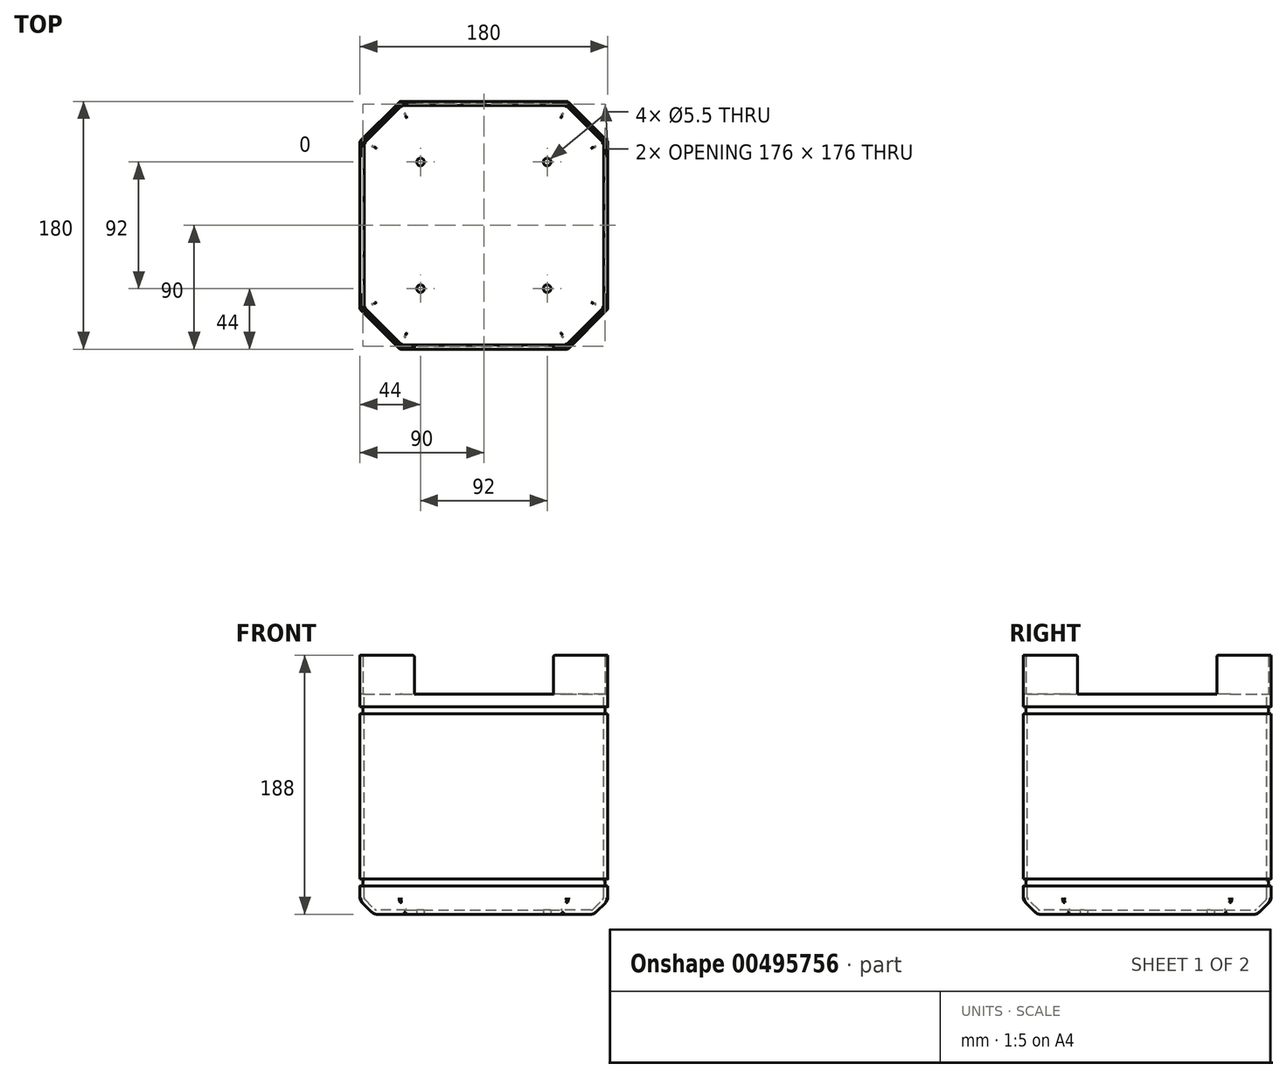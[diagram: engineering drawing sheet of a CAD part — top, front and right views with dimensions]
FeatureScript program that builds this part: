
annotation { "Feature Type Name" : "Feature", "Feature Type Description" : "" }
export const myFeature = defineFeature(function(context is Context, id is Id, definition is map)
    precondition{}
    {
        {
            var Q0;
            Q0=qCreatedBy(makeId("Top.planeOp"),FACE);
            var sketch = newSketch(context, id + "F0", { "sketchPlane" : qUnion([Q0])});
            skLineSegment(sketch, "E0.bottom", {"start": v(-61, 90) * mm, "end": v(61, 90) * mm});
            skLineSegment(sketch, "E0.top", {"start": v(-61, -90) * mm, "end": v(61, -90) * mm});
            skLineSegment(sketch, "E0.left", {"start": v(-90, 61) * mm, "end": v(-90, -61) * mm});
            skLineSegment(sketch, "E0.right", {"start": v(90, 61) * mm, "end": v(90, -61) * mm});
            skLineSegment(sketch, "E1", {"start": v(0, 156.9) * mm, "end": v(0, -146.72) * mm, "construction": true});
            skLineSegment(sketch, "E2", {"start": v(-149.43, 0) * mm, "end": v(169.81, 0) * mm, "construction": true});
            skLineSegment(sketch, "E3", {"start": v(-90, 61) * mm, "end": v(-61, 90) * mm});
            skLineSegment(sketch, "E4", {"start": v(-90, -61) * mm, "end": v(-61, -90) * mm});
            skLineSegment(sketch, "E5", {"start": v(61, -90) * mm, "end": v(90, -61) * mm});
            skLineSegment(sketch, "E6", {"start": v(61, 90) * mm, "end": v(90, 61) * mm});
            skPoint(sketch, "E7.orphan", {"position": v(-90, 90) * mm});
            skPoint(sketch, "E8.orphan", {"position": v(90, 90) * mm});
            skPoint(sketch, "E9.orphan", {"position": v(90, -90) * mm});
            skPoint(sketch, "E10.orphan", {"position": v(-90, -90) * mm});
            skSolve(sketch);
        }
        {
            var Q0;
            Q0=qSketchRegion(id+"F0",true);
            extrude(context, id + "F1", {"entities" : qUnion([Q0]), "depth" : 160 * mm, "offsetDistance" : 25 * mm});
        }
        {
            var Q0;
            Q0=makeQuery(id+"F1.opExtrude","CAP_EDGE",EDGE,{"disambiguationData":[OSD([sQuery(id+"F0.wireOp",EDGE,"E0.top")])],"isStart":true});
            var Q1;
            Q1=makeQuery(id+"F1.opExtrude","CAP_EDGE",EDGE,{"disambiguationData":[OSD([sQuery(id+"F0.wireOp",EDGE,"E4")])],"isStart":true});
            var Q2;
            Q2=makeQuery(id+"F1.opExtrude","CAP_EDGE",EDGE,{"disambiguationData":[OSD([sQuery(id+"F0.wireOp",EDGE,"E0.left")])],"isStart":true});
            var Q3;
            Q3=makeQuery(id+"F1.opExtrude","CAP_EDGE",EDGE,{"disambiguationData":[OSD([sQuery(id+"F0.wireOp",EDGE,"E3")])],"isStart":true});
            var Q4;
            Q4=makeQuery(id+"F1.opExtrude","CAP_EDGE",EDGE,{"disambiguationData":[OSD([sQuery(id+"F0.wireOp",EDGE,"E0.bottom")])],"isStart":true});
            var Q5;
            Q5=makeQuery(id+"F1.opExtrude","CAP_EDGE",EDGE,{"disambiguationData":[OSD([sQuery(id+"F0.wireOp",EDGE,"E6")])],"isStart":true});
            var Q6;
            Q6=makeQuery(id+"F1.opExtrude","CAP_EDGE",EDGE,{"disambiguationData":[OSD([sQuery(id+"F0.wireOp",EDGE,"E0.right")])],"isStart":true});
            var Q7;
            Q7=makeQuery(id+"F1.opExtrude","CAP_EDGE",EDGE,{"disambiguationData":[OSD([sQuery(id+"F0.wireOp",EDGE,"E5")])],"isStart":true});
            chamfer(context, id + "F2", {"entities" : qUnion([Q0, Q1, Q2, Q3, Q4, Q5, Q6, Q7]), "chamferType" : ChamferType.TWO_OFFSETS, "width1" : 10 * mm, "oppositeDirection" : true, "width2" : 10 * mm, "tangentPropagation" : true});
        }
        {
            var Q0;
            Q0=makeQuery(id+"F1.opExtrude","CAP_FACE",FACE,{"disambiguationData":[OSD([sQuery(id+"F0.wireOp",EDGE,"E0.bottom"),sQuery(id+"F0.wireOp",EDGE,"E0.top"),sQuery(id+"F0.wireOp",EDGE,"E0.left"),sQuery(id+"F0.wireOp",EDGE,"E0.right"),sQuery(id+"F0.wireOp",EDGE,"E3"),sQuery(id+"F0.wireOp",EDGE,"E4"),sQuery(id+"F0.wireOp",EDGE,"E5"),sQuery(id+"F0.wireOp",EDGE,"E6")])],"isStart":false});
            var sketch = newSketch(context, id + "F3", { "sketchPlane" : qUnion([Q0])});
            skLineSegment(sketch, "E11", {"start": v(90, -61) * mm, "end": v(61, -90) * mm});
            skLineSegment(sketch, "E12.0", {"start": v(88, -60.17) * mm, "end": v(60.17, -88) * mm});
            skLineSegment(sketch, "E13", {"start": v(90, -61) * mm, "end": v(90, -90) * mm, "construction": true});
            skLineSegment(sketch, "E14", {"start": v(90, -90) * mm, "end": v(61, -90) * mm, "construction": true});
            skLineSegment(sketch, "E15", {"start": v(90, -61) * mm, "end": v(90, -50.5) * mm});
            skLineSegment(sketch, "E16", {"start": v(61, -90) * mm, "end": v(50.5, -90) * mm});
            skLineSegment(sketch, "E17.0", {"start": v(60.17, -88) * mm, "end": v(50.5, -88) * mm});
            skLineSegment(sketch, "E18.0", {"start": v(88, -60.17) * mm, "end": v(88, -50.5) * mm});
            skLineSegment(sketch, "E19", {"start": v(88, -50.5) * mm, "end": v(90, -50.5) * mm});
            skLineSegment(sketch, "E20", {"start": v(50.5, -88) * mm, "end": v(50.5, -90) * mm});
            skLineSegment(sketch, "E21", {"start": v(104.54, 0) * mm, "end": v(-130.04, 0) * mm, "construction": true});
            skPoint(sketch, "E21.endSnap0", {"position": v(-90, 0) * mm});
            skLineSegment(sketch, "E22", {"start": v(0, 121.87) * mm, "end": v(0, -139.26) * mm, "construction": true});
            skLineSegment(sketch, "E23.MirrorCS", {"start": v(88, 50.5) * mm, "end": v(90, 50.5) * mm});
            skLineSegment(sketch, "E24.MirrorCS", {"start": v(50.5, 88) * mm, "end": v(50.5, 90) * mm});
            skLineSegment(sketch, "E25.MirrorCS", {"start": v(61, 90) * mm, "end": v(50.5, 90) * mm});
            skLineSegment(sketch, "E26.MirrorCS", {"start": v(60.17, 88) * mm, "end": v(50.5, 88) * mm});
            skLineSegment(sketch, "E27.MirrorCS", {"start": v(88, 60.17) * mm, "end": v(88, 50.5) * mm});
            skLineSegment(sketch, "E28.MirrorCS", {"start": v(90, 61) * mm, "end": v(90, 50.5) * mm});
            skLineSegment(sketch, "E29.MirrorCS", {"start": v(90, 61) * mm, "end": v(61, 90) * mm});
            skLineSegment(sketch, "E30.MirrorCS", {"start": v(88, 60.17) * mm, "end": v(60.17, 88) * mm});
            skLineSegment(sketch, "E31.MirrorCS", {"start": v(90, 90) * mm, "end": v(61, 90) * mm, "construction": true});
            skLineSegment(sketch, "E32.MirrorCS", {"start": v(90, 61) * mm, "end": v(90, 90) * mm, "construction": true});
            skLineSegment(sketch, "E33.MirrorCS", {"start": v(-88, 50.5) * mm, "end": v(-90, 50.5) * mm});
            skLineSegment(sketch, "E34.MirrorCS", {"start": v(-50.5, 88) * mm, "end": v(-50.5, 90) * mm});
            skLineSegment(sketch, "E35.MirrorCS", {"start": v(-88, -50.5) * mm, "end": v(-90, -50.5) * mm});
            skLineSegment(sketch, "E36.MirrorCS", {"start": v(-50.5, -88) * mm, "end": v(-50.5, -90) * mm});
            skLineSegment(sketch, "E37.MirrorCS", {"start": v(-61, -90) * mm, "end": v(-50.5, -90) * mm});
            skLineSegment(sketch, "E38.MirrorCS", {"start": v(-88, 60.17) * mm, "end": v(-88, 50.5) * mm});
            skLineSegment(sketch, "E39.MirrorCS", {"start": v(-61, 90) * mm, "end": v(-50.5, 90) * mm});
            skLineSegment(sketch, "E40.MirrorCS", {"start": v(-88, 60.17) * mm, "end": v(-60.17, 88) * mm});
            skLineSegment(sketch, "E41.MirrorCS", {"start": v(-88, -60.17) * mm, "end": v(-88, -50.5) * mm});
            skLineSegment(sketch, "E42.MirrorCS", {"start": v(-90, 61) * mm, "end": v(-61, 90) * mm});
            skLineSegment(sketch, "E43.MirrorCS", {"start": v(-60.17, 88) * mm, "end": v(-50.5, 88) * mm});
            skLineSegment(sketch, "E44.MirrorCS", {"start": v(-90, 61) * mm, "end": v(-90, 50.5) * mm});
            skLineSegment(sketch, "E45.MirrorCS", {"start": v(-90, -61) * mm, "end": v(-90, -50.5) * mm});
            skLineSegment(sketch, "E46.MirrorCS", {"start": v(-60.17, -88) * mm, "end": v(-50.5, -88) * mm});
            skLineSegment(sketch, "E47.MirrorCS", {"start": v(-90, 90) * mm, "end": v(-61, 90) * mm, "construction": true});
            skLineSegment(sketch, "E48.MirrorCS", {"start": v(-90, 61) * mm, "end": v(-90, 90) * mm, "construction": true});
            skLineSegment(sketch, "E49.MirrorCS", {"start": v(-90, -61) * mm, "end": v(-61, -90) * mm});
            skLineSegment(sketch, "E50.MirrorCS", {"start": v(-90, -61) * mm, "end": v(-90, -90) * mm, "construction": true});
            skLineSegment(sketch, "E51.MirrorCS", {"start": v(-90, -90) * mm, "end": v(-61, -90) * mm, "construction": true});
            skLineSegment(sketch, "E52.MirrorCS", {"start": v(-88, -60.17) * mm, "end": v(-60.17, -88) * mm});
            skSolve(sketch);
        }
        {
            var Q0;
            Q0=qSketchRegion(id+"F3",true);
            extrude(context, id + "F4", {"entities" : qUnion([Q0]), "operationType" : NewBodyOperationType.ADD, "depth" : 28 * mm});
        }
        {
            var Q0;
            {var subQ0=sQuery(id+"F0.wireOp",EDGE,"E6");Q0=makeQuery(id+"F2.opChamfer","BLEND_EDGE",EDGE,{"blendedFrom":[makeQuery(id+"F1.opExtrude","CAP_EDGE",EDGE,{"disambiguationData":[OSD([subQ0])],"isStart":true}),makeQuery(id+"F1.opExtrude","SWEPT_FACE",FACE,{"disambiguationData":[OSD([subQ0])]})],"blendedInto":[makeQuery(id+"F1.opExtrude","SWEPT_FACE",FACE,{"disambiguationData":[OSD([subQ0])]})]});}
            var Q1;
            {var subQ0=sQuery(id+"F0.wireOp",EDGE,"E0.right");Q1=makeQuery(id+"F2.opChamfer","BLEND_EDGE",EDGE,{"blendedFrom":[makeQuery(id+"F1.opExtrude","CAP_EDGE",EDGE,{"disambiguationData":[OSD([subQ0])],"isStart":true}),makeQuery(id+"F1.opExtrude","SWEPT_FACE",FACE,{"disambiguationData":[OSD([subQ0])]})],"blendedInto":[makeQuery(id+"F1.opExtrude","SWEPT_FACE",FACE,{"disambiguationData":[OSD([subQ0])]})]});}
            var Q2;
            {var subQ0=sQuery(id+"F0.wireOp",EDGE,"E5");Q2=makeQuery(id+"F2.opChamfer","BLEND_EDGE",EDGE,{"blendedFrom":[makeQuery(id+"F1.opExtrude","CAP_EDGE",EDGE,{"disambiguationData":[OSD([subQ0])],"isStart":true}),makeQuery(id+"F1.opExtrude","SWEPT_FACE",FACE,{"disambiguationData":[OSD([subQ0])]})],"blendedInto":[makeQuery(id+"F1.opExtrude","SWEPT_FACE",FACE,{"disambiguationData":[OSD([subQ0])]})]});}
            var Q3;
            {var subQ0=sQuery(id+"F0.wireOp",EDGE,"E0.top");Q3=makeQuery(id+"F2.opChamfer","BLEND_EDGE",EDGE,{"blendedFrom":[makeQuery(id+"F1.opExtrude","CAP_EDGE",EDGE,{"disambiguationData":[OSD([subQ0])],"isStart":true}),makeQuery(id+"F1.opExtrude","SWEPT_FACE",FACE,{"disambiguationData":[OSD([subQ0])]})],"blendedInto":[makeQuery(id+"F1.opExtrude","SWEPT_FACE",FACE,{"disambiguationData":[OSD([subQ0])]})]});}
            var Q4;
            {var subQ0=sQuery(id+"F0.wireOp",EDGE,"E4");Q4=makeQuery(id+"F2.opChamfer","BLEND_EDGE",EDGE,{"blendedFrom":[makeQuery(id+"F1.opExtrude","CAP_EDGE",EDGE,{"disambiguationData":[OSD([subQ0])],"isStart":true}),makeQuery(id+"F1.opExtrude","SWEPT_FACE",FACE,{"disambiguationData":[OSD([subQ0])]})],"blendedInto":[makeQuery(id+"F1.opExtrude","SWEPT_FACE",FACE,{"disambiguationData":[OSD([subQ0])]})]});}
            var Q5;
            {var subQ0=sQuery(id+"F0.wireOp",EDGE,"E0.left");Q5=makeQuery(id+"F2.opChamfer","BLEND_EDGE",EDGE,{"blendedFrom":[makeQuery(id+"F1.opExtrude","CAP_EDGE",EDGE,{"disambiguationData":[OSD([subQ0])],"isStart":true}),makeQuery(id+"F1.opExtrude","SWEPT_FACE",FACE,{"disambiguationData":[OSD([subQ0])]})],"blendedInto":[makeQuery(id+"F1.opExtrude","SWEPT_FACE",FACE,{"disambiguationData":[OSD([subQ0])]})]});}
            var Q6;
            {var subQ0=sQuery(id+"F0.wireOp",EDGE,"E3");Q6=makeQuery(id+"F2.opChamfer","BLEND_EDGE",EDGE,{"blendedFrom":[makeQuery(id+"F1.opExtrude","CAP_EDGE",EDGE,{"disambiguationData":[OSD([subQ0])],"isStart":true}),makeQuery(id+"F1.opExtrude","SWEPT_FACE",FACE,{"disambiguationData":[OSD([subQ0])]})],"blendedInto":[makeQuery(id+"F1.opExtrude","SWEPT_FACE",FACE,{"disambiguationData":[OSD([subQ0])]})]});}
            var Q7;
            {var subQ0=sQuery(id+"F0.wireOp",EDGE,"E0.bottom");Q7=makeQuery(id+"F2.opChamfer","BLEND_EDGE",EDGE,{"blendedFrom":[makeQuery(id+"F1.opExtrude","CAP_EDGE",EDGE,{"disambiguationData":[OSD([subQ0])],"isStart":true}),makeQuery(id+"F1.opExtrude","SWEPT_FACE",FACE,{"disambiguationData":[OSD([subQ0])]})],"blendedInto":[makeQuery(id+"F1.opExtrude","SWEPT_FACE",FACE,{"disambiguationData":[OSD([subQ0])]})]});}
            fillet(context, id + "F5", {"entities" : qUnion([Q0, Q1, Q2, Q3, Q4, Q5, Q6, Q7]), "radius" : 5 * mm, "tangentPropagation" : true, "allowEdgeOverflow" : false});
        }
        {
            var Q0;
            Q0=makeQuery(id+"F4.boolean.opBoolean","MERGE",EDGE,{"derivedFrom":[makeQuery(id+"F1.opExtrude","SWEPT_EDGE",EDGE,{"disambiguationData":[OSD([sQuery(id+"F0.wireOp",EDGE,"E0.bottom"),sQuery(id+"F0.wireOp",EDGE,"E6")])]}),makeQuery(id+"F4.opExtrude","SWEPT_EDGE",EDGE,{"disambiguationData":[OSD([sQuery(id+"F3.wireOp",EDGE,"E25.MirrorCS"),sQuery(id+"F3.wireOp",EDGE,"E29.MirrorCS")])]})]});
            var Q1;
            Q1=makeQuery(id+"F4.boolean.opBoolean","MERGE",EDGE,{"derivedFrom":[makeQuery(id+"F1.opExtrude","SWEPT_EDGE",EDGE,{"disambiguationData":[OSD([sQuery(id+"F0.wireOp",EDGE,"E0.right"),sQuery(id+"F0.wireOp",EDGE,"E6")])]}),makeQuery(id+"F4.opExtrude","SWEPT_EDGE",EDGE,{"disambiguationData":[OSD([sQuery(id+"F3.wireOp",EDGE,"E28.MirrorCS"),sQuery(id+"F3.wireOp",EDGE,"E29.MirrorCS")])]})]});
            var Q2;
            Q2=makeQuery(id+"F4.boolean.opBoolean","MERGE",EDGE,{"derivedFrom":[makeQuery(id+"F1.opExtrude","SWEPT_EDGE",EDGE,{"disambiguationData":[OSD([sQuery(id+"F0.wireOp",EDGE,"E0.bottom"),sQuery(id+"F0.wireOp",EDGE,"E3")])]}),makeQuery(id+"F4.opExtrude","SWEPT_EDGE",EDGE,{"disambiguationData":[OSD([sQuery(id+"F3.wireOp",EDGE,"E39.MirrorCS"),sQuery(id+"F3.wireOp",EDGE,"E42.MirrorCS")])]})]});
            var Q3;
            Q3=makeQuery(id+"F4.boolean.opBoolean","MERGE",EDGE,{"derivedFrom":[makeQuery(id+"F1.opExtrude","SWEPT_EDGE",EDGE,{"disambiguationData":[OSD([sQuery(id+"F0.wireOp",EDGE,"E0.right"),sQuery(id+"F0.wireOp",EDGE,"E5")])]}),makeQuery(id+"F4.opExtrude","SWEPT_EDGE",EDGE,{"disambiguationData":[OSD([sQuery(id+"F3.wireOp",EDGE,"E11"),sQuery(id+"F3.wireOp",EDGE,"E15")])]})]});
            var Q4;
            Q4=makeQuery(id+"F2.opChamfer","BLEND_EDGE",EDGE,{"blendedFrom":[makeQuery(id+"F1.opExtrude","CAP_EDGE",EDGE,{"disambiguationData":[OSD([sQuery(id+"F0.wireOp",EDGE,"E0.top")])],"isStart":true}),makeQuery(id+"F1.opExtrude","CAP_EDGE",EDGE,{"disambiguationData":[OSD([sQuery(id+"F0.wireOp",EDGE,"E5")])],"isStart":true})],"blendedInto":[]});
            var Q5;
            Q5=makeQuery(id+"F2.opChamfer","BLEND_EDGE",EDGE,{"blendedFrom":[makeQuery(id+"F1.opExtrude","CAP_EDGE",EDGE,{"disambiguationData":[OSD([sQuery(id+"F0.wireOp",EDGE,"E0.top")])],"isStart":true}),makeQuery(id+"F1.opExtrude","CAP_EDGE",EDGE,{"disambiguationData":[OSD([sQuery(id+"F0.wireOp",EDGE,"E4")])],"isStart":true})],"blendedInto":[]});
            var Q6;
            Q6=makeQuery(id+"F2.opChamfer","BLEND_EDGE",EDGE,{"blendedFrom":[makeQuery(id+"F1.opExtrude","CAP_EDGE",EDGE,{"disambiguationData":[OSD([sQuery(id+"F0.wireOp",EDGE,"E0.left")])],"isStart":true}),makeQuery(id+"F1.opExtrude","CAP_EDGE",EDGE,{"disambiguationData":[OSD([sQuery(id+"F0.wireOp",EDGE,"E4")])],"isStart":true})],"blendedInto":[]});
            var Q7;
            Q7=makeQuery(id+"F2.opChamfer","BLEND_EDGE",EDGE,{"blendedFrom":[makeQuery(id+"F1.opExtrude","CAP_EDGE",EDGE,{"disambiguationData":[OSD([sQuery(id+"F0.wireOp",EDGE,"E0.left")])],"isStart":true}),makeQuery(id+"F1.opExtrude","CAP_EDGE",EDGE,{"disambiguationData":[OSD([sQuery(id+"F0.wireOp",EDGE,"E3")])],"isStart":true})],"blendedInto":[]});
            fillet(context, id + "F6", {"entities" : qUnion([Q0, Q1, Q2, Q3, Q4, Q5, Q6, Q7]), "radius" : 2 * mm, "tangentPropagation" : true, "allowEdgeOverflow" : false});
        }
        {
            var Q0;
            {var subQ0=sQuery(id+"F0.wireOp",EDGE,"E0.left");Q0=makeQuery(id+"F2.opChamfer","BLEND_EDGE",EDGE,{"blendedFrom":[makeQuery(id+"F1.opExtrude","CAP_EDGE",EDGE,{"disambiguationData":[OSD([subQ0])],"isStart":true}),makeQuery(id+"F1.opExtrude","CAP_FACE",FACE,{"disambiguationData":[OSD([sQuery(id+"F0.wireOp",EDGE,"E0.bottom"),sQuery(id+"F0.wireOp",EDGE,"E0.top"),subQ0,sQuery(id+"F0.wireOp",EDGE,"E0.right"),sQuery(id+"F0.wireOp",EDGE,"E3"),sQuery(id+"F0.wireOp",EDGE,"E4"),sQuery(id+"F0.wireOp",EDGE,"E5"),sQuery(id+"F0.wireOp",EDGE,"E6")])],"isStart":true})],"blendedInto":[makeQuery(id+"F1.opExtrude","CAP_FACE",FACE,{"disambiguationData":[OSD([sQuery(id+"F0.wireOp",EDGE,"E0.bottom"),sQuery(id+"F0.wireOp",EDGE,"E0.top"),subQ0,sQuery(id+"F0.wireOp",EDGE,"E0.right"),sQuery(id+"F0.wireOp",EDGE,"E3"),sQuery(id+"F0.wireOp",EDGE,"E4"),sQuery(id+"F0.wireOp",EDGE,"E5"),sQuery(id+"F0.wireOp",EDGE,"E6")])],"isStart":true})]});}
            fillet(context, id + "F7", {"entities" : qUnion([Q0]), "radius" : 5 * mm, "tangentPropagation" : true, "allowEdgeOverflow" : false});
        }
        {
            var Q0;
            Q0=makeQuery(id+"F1.opExtrude","CAP_FACE",FACE,{"disambiguationData":[OSD([sQuery(id+"F0.wireOp",EDGE,"E0.bottom"),sQuery(id+"F0.wireOp",EDGE,"E0.top"),sQuery(id+"F0.wireOp",EDGE,"E0.left"),sQuery(id+"F0.wireOp",EDGE,"E0.right"),sQuery(id+"F0.wireOp",EDGE,"E3"),sQuery(id+"F0.wireOp",EDGE,"E4"),sQuery(id+"F0.wireOp",EDGE,"E5"),sQuery(id+"F0.wireOp",EDGE,"E6")])],"isStart":false});
            shell(context, id + "F8", {"entities" : qUnion([Q0]), "thickness" : 3 * mm});
        }
        {
            var Q0;
            Q0=qCreatedBy(makeId("Front.planeOp"),FACE);
            var sketch = newSketch(context, id + "F9", { "sketchPlane" : qUnion([Q0])});
            skLineSegment(sketch, "E53.bottom", {"start": v(109.07, 145.57) * mm, "end": v(-112.92, 145.57) * mm});
            skLineSegment(sketch, "E53.top", {"start": v(109.07, 150.57) * mm, "end": v(-112.92, 150.57) * mm});
            skLineSegment(sketch, "E53.left", {"start": v(109.07, 145.57) * mm, "end": v(109.07, 150.57) * mm});
            skLineSegment(sketch, "E53.right", {"start": v(-112.92, 145.57) * mm, "end": v(-112.92, 150.57) * mm});
            skLineSegment(sketch, "E54.bottom", {"start": v(124, 20.57) * mm, "end": v(-129.94, 20.57) * mm});
            skLineSegment(sketch, "E54.top", {"start": v(124, 25.57) * mm, "end": v(-129.94, 25.57) * mm});
            skLineSegment(sketch, "E54.left", {"start": v(124, 20.57) * mm, "end": v(124, 25.57) * mm});
            skLineSegment(sketch, "E54.right", {"start": v(-129.94, 20.57) * mm, "end": v(-129.94, 25.57) * mm});
            skSolve(sketch);
        }
        {
            var Q0;
            Q0 = qSketchRegion(id + "F9", true);
            extrude(context, id + "F10", {"entities" : qUnion([Q0]), "operationType" : NewBodyOperationType.REMOVE, "oppositeDirection" : true, "depth" : 180 * mm, "symmetric" : true});
        }
        {
            var Q0;
            Q0=makeQuery(id+"F10.boolean.opBoolean","COPY",FACE,{"derivedFrom":makeQuery(id+"F10.opExtrude","SWEPT_FACE",FACE,{"disambiguationData":[OSD([sQuery(id+"F9.wireOp",EDGE,"E54.bottom")])]})});
            var sketch = newSketch(context, id + "F11", { "sketchPlane" : qUnion([Q0])});
            skLineSegment(sketch, "E55.0", {"start": v(-60.17, -88) * mm, "end": v(60.17, -88) * mm});
            skLineSegment(sketch, "E55.1", {"start": v(-88, -60.17) * mm, "end": v(-60.17, -88) * mm});
            skLineSegment(sketch, "E55.2", {"start": v(60.17, -88) * mm, "end": v(88, -60.17) * mm});
            skLineSegment(sketch, "E55.3", {"start": v(-88, 60.17) * mm, "end": v(-88, -60.17) * mm});
            skLineSegment(sketch, "E55.4", {"start": v(88, -60.17) * mm, "end": v(88, 60.17) * mm});
            skLineSegment(sketch, "E55.5", {"start": v(88, 60.17) * mm, "end": v(60.17, 88) * mm});
            skLineSegment(sketch, "E55.6", {"start": v(60.17, 88) * mm, "end": v(-60.17, 88) * mm});
            skLineSegment(sketch, "E55.7", {"start": v(-60.17, 88) * mm, "end": v(-88, 60.17) * mm});
            skLineSegment(sketch, "E56.0", {"start": v(-59.76, 87) * mm, "end": v(-59.76, 87) * mm});
            skLineSegment(sketch, "E56.2", {"start": v(-87, 59.76) * mm, "end": v(-87, -59.76) * mm});
            skLineSegment(sketch, "E56.4", {"start": v(-59.76, 87) * mm, "end": v(59.76, 87) * mm});
            skLineSegment(sketch, "E56.6", {"start": v(59.76, 87) * mm, "end": v(59.76, 87) * mm});
            skLineSegment(sketch, "E56.8", {"start": v(87, 59.76) * mm, "end": v(87, -59.76) * mm});
            skLineSegment(sketch, "E56.10", {"start": v(59.76, -87) * mm, "end": v(59.76, -87) * mm});
            skLineSegment(sketch, "E56.12", {"start": v(-59.76, -87) * mm, "end": v(59.76, -87) * mm});
            skLineSegment(sketch, "E56.14", {"start": v(-59.76, -87) * mm, "end": v(-59.76, -87) * mm});
            skLineSegment(sketch, "E57", {"start": v(87, 59.76) * mm, "end": v(59.76, 87) * mm});
            skLineSegment(sketch, "E58", {"start": v(-59.76, 87) * mm, "end": v(-87, 59.76) * mm});
            skLineSegment(sketch, "E59", {"start": v(-59.76, -87) * mm, "end": v(-87, -59.76) * mm});
            skLineSegment(sketch, "E60", {"start": v(87, -59.76) * mm, "end": v(59.76, -87) * mm});
            skSolve(sketch);
        }
        {
            var Q0;
            Q0 = qSketchRegion(id + "F11", true);
            extrude(context, id + "F12", {"entities" : qUnion([Q0]), "operationType" : NewBodyOperationType.ADD, "depth" : 130 * mm});
        }
        {
            var Q0;
            {var subQ0=sQuery(id+"F11.wireOp",EDGE,"E55.7");var subQ1=sQuery(id+"F11.wireOp",EDGE,"E55.3");Q0=makeQuery(id+"F12.boolean.opBoolean","SPLIT",EDGE,{"disambiguationData":[TD([makeQuery(id+"F10.boolean.opBoolean","COPY",FACE,{"derivedFrom":makeQuery(id+"F10.opExtrude","SWEPT_FACE",FACE,{"disambiguationData":[OSD([sQuery(id+"F9.wireOp",EDGE,"E54.bottom")])]})})])],"derivedFrom":makeQuery(id+"F12.opExtrude","SWEPT_EDGE",EDGE,{"disambiguationData":[OSD([subQ1,subQ0])]})});}
            var Q1;
            {var subQ0=sQuery(id+"F11.wireOp",EDGE,"E55.7");var subQ1=sQuery(id+"F11.wireOp",EDGE,"E55.6");Q1=makeQuery(id+"F12.boolean.opBoolean","SPLIT",EDGE,{"disambiguationData":[TD([makeQuery(id+"F10.boolean.opBoolean","COPY",FACE,{"derivedFrom":makeQuery(id+"F10.opExtrude","SWEPT_FACE",FACE,{"disambiguationData":[OSD([sQuery(id+"F9.wireOp",EDGE,"E54.bottom")])]})})])],"derivedFrom":makeQuery(id+"F12.opExtrude","SWEPT_EDGE",EDGE,{"disambiguationData":[OSD([subQ1,subQ0])]})});}
            var Q2;
            {var subQ0=sQuery(id+"F11.wireOp",EDGE,"E55.5");var subQ1=sQuery(id+"F11.wireOp",EDGE,"E55.6");Q2=makeQuery(id+"F12.boolean.opBoolean","SPLIT",EDGE,{"disambiguationData":[TD([makeQuery(id+"F10.boolean.opBoolean","COPY",FACE,{"derivedFrom":makeQuery(id+"F10.opExtrude","SWEPT_FACE",FACE,{"disambiguationData":[OSD([sQuery(id+"F9.wireOp",EDGE,"E54.bottom")])]})})])],"derivedFrom":makeQuery(id+"F12.opExtrude","SWEPT_EDGE",EDGE,{"disambiguationData":[OSD([subQ0,subQ1])]})});}
            var Q3;
            {var subQ0=sQuery(id+"F11.wireOp",EDGE,"E55.5");var subQ1=sQuery(id+"F11.wireOp",EDGE,"E55.6");Q3=makeQuery(id+"F12.boolean.opBoolean","SPLIT",EDGE,{"disambiguationData":[TD([makeQuery(id+"F10.boolean.opBoolean","COPY",FACE,{"derivedFrom":makeQuery(id+"F10.opExtrude","SWEPT_FACE",FACE,{"disambiguationData":[OSD([sQuery(id+"F9.wireOp",EDGE,"E53.bottom")])]})})])],"derivedFrom":makeQuery(id+"F12.opExtrude","SWEPT_EDGE",EDGE,{"disambiguationData":[OSD([subQ0,subQ1])]})});}
            var Q4;
            {var subQ0=sQuery(id+"F11.wireOp",EDGE,"E55.6");var subQ1=sQuery(id+"F11.wireOp",EDGE,"E55.7");Q4=makeQuery(id+"F12.boolean.opBoolean","SPLIT",EDGE,{"disambiguationData":[TD([makeQuery(id+"F10.boolean.opBoolean","COPY",FACE,{"derivedFrom":makeQuery(id+"F10.opExtrude","SWEPT_FACE",FACE,{"disambiguationData":[OSD([sQuery(id+"F9.wireOp",EDGE,"E53.bottom")])]})})])],"derivedFrom":makeQuery(id+"F12.opExtrude","SWEPT_EDGE",EDGE,{"disambiguationData":[OSD([subQ0,subQ1])]})});}
            var Q5;
            {var subQ0=sQuery(id+"F11.wireOp",EDGE,"E55.3");var subQ1=sQuery(id+"F11.wireOp",EDGE,"E55.7");Q5=makeQuery(id+"F12.boolean.opBoolean","SPLIT",EDGE,{"disambiguationData":[TD([makeQuery(id+"F10.boolean.opBoolean","COPY",FACE,{"derivedFrom":makeQuery(id+"F10.opExtrude","SWEPT_FACE",FACE,{"disambiguationData":[OSD([sQuery(id+"F9.wireOp",EDGE,"E53.bottom")])]})})])],"derivedFrom":makeQuery(id+"F12.opExtrude","SWEPT_EDGE",EDGE,{"disambiguationData":[OSD([subQ0,subQ1])]})});}
            var Q6;
            {var subQ0=sQuery(id+"F11.wireOp",EDGE,"E55.5");var subQ1=sQuery(id+"F11.wireOp",EDGE,"E55.4");Q6=makeQuery(id+"F12.boolean.opBoolean","SPLIT",EDGE,{"disambiguationData":[TD([makeQuery(id+"F10.boolean.opBoolean","COPY",FACE,{"derivedFrom":makeQuery(id+"F10.opExtrude","SWEPT_FACE",FACE,{"disambiguationData":[OSD([sQuery(id+"F9.wireOp",EDGE,"E53.bottom")])]})})])],"derivedFrom":makeQuery(id+"F12.opExtrude","SWEPT_EDGE",EDGE,{"disambiguationData":[OSD([subQ1,subQ0])]})});}
            var Q7;
            {var subQ0=sQuery(id+"F11.wireOp",EDGE,"E55.4");var subQ1=sQuery(id+"F11.wireOp",EDGE,"E55.5");Q7=makeQuery(id+"F12.boolean.opBoolean","SPLIT",EDGE,{"disambiguationData":[TD([makeQuery(id+"F10.boolean.opBoolean","COPY",FACE,{"derivedFrom":makeQuery(id+"F10.opExtrude","SWEPT_FACE",FACE,{"disambiguationData":[OSD([sQuery(id+"F9.wireOp",EDGE,"E54.bottom")])]})})])],"derivedFrom":makeQuery(id+"F12.opExtrude","SWEPT_EDGE",EDGE,{"disambiguationData":[OSD([subQ0,subQ1])]})});}
            var Q8;
            {var subQ0=sQuery(id+"F11.wireOp",EDGE,"E55.2");var subQ1=sQuery(id+"F11.wireOp",EDGE,"E55.4");Q8=makeQuery(id+"F12.boolean.opBoolean","SPLIT",EDGE,{"disambiguationData":[TD([makeQuery(id+"F10.boolean.opBoolean","COPY",FACE,{"derivedFrom":makeQuery(id+"F10.opExtrude","SWEPT_FACE",FACE,{"disambiguationData":[OSD([sQuery(id+"F9.wireOp",EDGE,"E54.bottom")])]})})])],"derivedFrom":makeQuery(id+"F12.opExtrude","SWEPT_EDGE",EDGE,{"disambiguationData":[OSD([subQ0,subQ1])]})});}
            var Q9;
            {var subQ0=sQuery(id+"F11.wireOp",EDGE,"E55.2");var subQ1=sQuery(id+"F11.wireOp",EDGE,"E55.0");Q9=makeQuery(id+"F12.boolean.opBoolean","SPLIT",EDGE,{"disambiguationData":[TD([makeQuery(id+"F10.boolean.opBoolean","COPY",FACE,{"derivedFrom":makeQuery(id+"F10.opExtrude","SWEPT_FACE",FACE,{"disambiguationData":[OSD([sQuery(id+"F9.wireOp",EDGE,"E54.bottom")])]})})])],"derivedFrom":makeQuery(id+"F12.opExtrude","SWEPT_EDGE",EDGE,{"disambiguationData":[OSD([subQ1,subQ0])]})});}
            var Q10;
            {var subQ0=sQuery(id+"F11.wireOp",EDGE,"E55.2");var subQ1=sQuery(id+"F11.wireOp",EDGE,"E55.4");Q10=makeQuery(id+"F12.boolean.opBoolean","SPLIT",EDGE,{"disambiguationData":[TD([makeQuery(id+"F10.boolean.opBoolean","COPY",FACE,{"derivedFrom":makeQuery(id+"F10.opExtrude","SWEPT_FACE",FACE,{"disambiguationData":[OSD([sQuery(id+"F9.wireOp",EDGE,"E53.bottom")])]})})])],"derivedFrom":makeQuery(id+"F12.opExtrude","SWEPT_EDGE",EDGE,{"disambiguationData":[OSD([subQ0,subQ1])]})});}
            var Q11;
            {var subQ0=sQuery(id+"F11.wireOp",EDGE,"E55.0");var subQ1=sQuery(id+"F11.wireOp",EDGE,"E55.2");Q11=makeQuery(id+"F12.boolean.opBoolean","SPLIT",EDGE,{"disambiguationData":[TD([makeQuery(id+"F10.boolean.opBoolean","COPY",FACE,{"derivedFrom":makeQuery(id+"F10.opExtrude","SWEPT_FACE",FACE,{"disambiguationData":[OSD([sQuery(id+"F9.wireOp",EDGE,"E53.bottom")])]})})])],"derivedFrom":makeQuery(id+"F12.opExtrude","SWEPT_EDGE",EDGE,{"disambiguationData":[OSD([subQ0,subQ1])]})});}
            var Q12;
            {var subQ0=sQuery(id+"F11.wireOp",EDGE,"E55.0");var subQ1=sQuery(id+"F11.wireOp",EDGE,"E55.1");Q12=makeQuery(id+"F12.boolean.opBoolean","SPLIT",EDGE,{"disambiguationData":[TD([makeQuery(id+"F10.boolean.opBoolean","COPY",FACE,{"derivedFrom":makeQuery(id+"F10.opExtrude","SWEPT_FACE",FACE,{"disambiguationData":[OSD([sQuery(id+"F9.wireOp",EDGE,"E54.bottom")])]})})])],"derivedFrom":makeQuery(id+"F12.opExtrude","SWEPT_EDGE",EDGE,{"disambiguationData":[OSD([subQ0,subQ1])]})});}
            var Q13;
            {var subQ0=sQuery(id+"F11.wireOp",EDGE,"E55.3");var subQ1=sQuery(id+"F11.wireOp",EDGE,"E55.1");Q13=makeQuery(id+"F12.boolean.opBoolean","SPLIT",EDGE,{"disambiguationData":[TD([makeQuery(id+"F10.boolean.opBoolean","COPY",FACE,{"derivedFrom":makeQuery(id+"F10.opExtrude","SWEPT_FACE",FACE,{"disambiguationData":[OSD([sQuery(id+"F9.wireOp",EDGE,"E54.bottom")])]})})])],"derivedFrom":makeQuery(id+"F12.opExtrude","SWEPT_EDGE",EDGE,{"disambiguationData":[OSD([subQ1,subQ0])]})});}
            var Q14;
            {var subQ0=sQuery(id+"F11.wireOp",EDGE,"E55.1");var subQ1=sQuery(id+"F11.wireOp",EDGE,"E55.0");Q14=makeQuery(id+"F12.boolean.opBoolean","SPLIT",EDGE,{"disambiguationData":[TD([makeQuery(id+"F10.boolean.opBoolean","COPY",FACE,{"derivedFrom":makeQuery(id+"F10.opExtrude","SWEPT_FACE",FACE,{"disambiguationData":[OSD([sQuery(id+"F9.wireOp",EDGE,"E53.bottom")])]})})])],"derivedFrom":makeQuery(id+"F12.opExtrude","SWEPT_EDGE",EDGE,{"disambiguationData":[OSD([subQ1,subQ0])]})});}
            var Q15;
            {var subQ0=sQuery(id+"F11.wireOp",EDGE,"E55.1");var subQ1=sQuery(id+"F11.wireOp",EDGE,"E55.3");Q15=makeQuery(id+"F12.boolean.opBoolean","SPLIT",EDGE,{"disambiguationData":[TD([makeQuery(id+"F10.boolean.opBoolean","COPY",FACE,{"derivedFrom":makeQuery(id+"F10.opExtrude","SWEPT_FACE",FACE,{"disambiguationData":[OSD([sQuery(id+"F9.wireOp",EDGE,"E53.bottom")])]})})])],"derivedFrom":makeQuery(id+"F12.opExtrude","SWEPT_EDGE",EDGE,{"disambiguationData":[OSD([subQ0,subQ1])]})});}
            fillet(context, id + "F13", {"entities" : qUnion([Q0, Q1, Q2, Q3, Q4, Q5, Q6, Q7, Q8, Q9, Q10, Q11, Q12, Q13, Q14, Q15]), "radius" : 2 * mm, "tangentPropagation" : true, "allowEdgeOverflow" : false});
        }
        {
            var Q0;
            Q0=makeQuery(id+"F1.opExtrude","CAP_FACE",FACE,{"disambiguationData":[OSD([sQuery(id+"F0.wireOp",EDGE,"E0.bottom"),sQuery(id+"F0.wireOp",EDGE,"E0.top"),sQuery(id+"F0.wireOp",EDGE,"E0.left"),sQuery(id+"F0.wireOp",EDGE,"E0.right"),sQuery(id+"F0.wireOp",EDGE,"E3"),sQuery(id+"F0.wireOp",EDGE,"E4"),sQuery(id+"F0.wireOp",EDGE,"E5"),sQuery(id+"F0.wireOp",EDGE,"E6")])],"isStart":true});
            var sketch = newSketch(context, id + "F14", { "sketchPlane" : qUnion([Q0])});
            skLineSegment(sketch, "E61", {"start": v(0, 77.93) * mm, "end": v(0, -77.93) * mm, "construction": true});
            skLineSegment(sketch, "E62", {"start": v(-77.93, 0) * mm, "end": v(77.93, 0) * mm, "construction": true});
            skLineSegment(sketch, "E63", {"start": v(-66.96, -66.96) * mm, "end": v(66.96, 66.96) * mm, "construction": true});
            skLineSegment(sketch, "E64", {"start": v(-66.96, 66.96) * mm, "end": v(66.96, -66.96) * mm, "construction": true});
            skCircle(sketch, "E65", {"center": v(-46, -46) * mm, "radius": 2.75 * mm});
            skCircle(sketch, "E66", {"center": v(-46, 46) * mm, "radius": 2.75 * mm});
            skCircle(sketch, "E67", {"center": v(46, 46) * mm, "radius": 2.75 * mm});
            skCircle(sketch, "E68", {"center": v(46, -46) * mm, "radius": 2.75 * mm});
            skSolve(sketch);
        }
        {
            var Q0;
            Q0 = qSketchRegion(id + "F14", true);
            extrude(context, id + "F15", {"entities" : qUnion([Q0]), "operationType" : NewBodyOperationType.REMOVE, "oppositeDirection" : true, "depth" : 25 * mm});
        }
        {
            var Q0;
            Q0=makeQuery(id+"F4.opExtrude","SWEPT_EDGE",EDGE,{"disambiguationData":[OSD([sQuery(id+"F3.wireOp",EDGE,"E41.MirrorCS"),sQuery(id+"F3.wireOp",EDGE,"E52.MirrorCS")])]});
            var Q1;
            Q1=makeQuery(id+"F4.opExtrude","SWEPT_EDGE",EDGE,{"disambiguationData":[OSD([sQuery(id+"F3.wireOp",EDGE,"E46.MirrorCS"),sQuery(id+"F3.wireOp",EDGE,"E52.MirrorCS")])]});
            var Q2;
            Q2=makeQuery(id+"F4.opExtrude","SWEPT_EDGE",EDGE,{"disambiguationData":[OSD([sQuery(id+"F3.wireOp",EDGE,"E12.0"),sQuery(id+"F3.wireOp",EDGE,"E18.0")])]});
            var Q3;
            Q3=makeQuery(id+"F4.opExtrude","SWEPT_EDGE",EDGE,{"disambiguationData":[OSD([sQuery(id+"F3.wireOp",EDGE,"E12.0"),sQuery(id+"F3.wireOp",EDGE,"E17.0")])]});
            var Q4;
            Q4=makeQuery(id+"F4.opExtrude","SWEPT_EDGE",EDGE,{"disambiguationData":[OSD([sQuery(id+"F3.wireOp",EDGE,"E27.MirrorCS"),sQuery(id+"F3.wireOp",EDGE,"E30.MirrorCS")])]});
            var Q5;
            Q5=makeQuery(id+"F4.opExtrude","SWEPT_EDGE",EDGE,{"disambiguationData":[OSD([sQuery(id+"F3.wireOp",EDGE,"E26.MirrorCS"),sQuery(id+"F3.wireOp",EDGE,"E30.MirrorCS")])]});
            var Q6;
            Q6=makeQuery(id+"F4.opExtrude","SWEPT_EDGE",EDGE,{"disambiguationData":[OSD([sQuery(id+"F3.wireOp",EDGE,"E43.MirrorCS"),sQuery(id+"F3.wireOp",EDGE,"E40.MirrorCS")])]});
            var Q7;
            Q7=makeQuery(id+"F4.opExtrude","SWEPT_EDGE",EDGE,{"disambiguationData":[OSD([sQuery(id+"F3.wireOp",EDGE,"E38.MirrorCS"),sQuery(id+"F3.wireOp",EDGE,"E40.MirrorCS")])]});
            fillet(context, id + "F16", {"entities" : qUnion([Q0, Q1, Q2, Q3, Q4, Q5, Q6, Q7]), "radius" : 2 * mm, "tangentPropagation" : true, "allowEdgeOverflow" : false});
        }
        {
            var Q0;
            Q0=makeQuery(id+"F4.opExtrude","CAP_EDGE",EDGE,{"disambiguationData":[OSD([sQuery(id+"F3.wireOp",EDGE,"E35.MirrorCS")])],"isStart":false});
            var Q1;
            Q1=makeQuery(id+"F4.opExtrude","CAP_EDGE",EDGE,{"disambiguationData":[OSD([sQuery(id+"F3.wireOp",EDGE,"E36.MirrorCS")])],"isStart":false});
            var Q2;
            Q2=makeQuery(id+"F4.opExtrude","CAP_EDGE",EDGE,{"disambiguationData":[OSD([sQuery(id+"F3.wireOp",EDGE,"E20")])],"isStart":false});
            var Q3;
            Q3=makeQuery(id+"F4.opExtrude","CAP_EDGE",EDGE,{"disambiguationData":[OSD([sQuery(id+"F3.wireOp",EDGE,"E19")])],"isStart":false});
            var Q4;
            Q4=makeQuery(id+"F4.opExtrude","CAP_EDGE",EDGE,{"disambiguationData":[OSD([sQuery(id+"F3.wireOp",EDGE,"E23.MirrorCS")])],"isStart":false});
            var Q5;
            Q5=makeQuery(id+"F4.opExtrude","CAP_EDGE",EDGE,{"disambiguationData":[OSD([sQuery(id+"F3.wireOp",EDGE,"E24.MirrorCS")])],"isStart":false});
            var Q6;
            Q6=makeQuery(id+"F4.opExtrude","CAP_EDGE",EDGE,{"disambiguationData":[OSD([sQuery(id+"F3.wireOp",EDGE,"E34.MirrorCS")])],"isStart":false});
            var Q7;
            Q7=makeQuery(id+"F4.opExtrude","CAP_EDGE",EDGE,{"disambiguationData":[OSD([sQuery(id+"F3.wireOp",EDGE,"E33.MirrorCS")])],"isStart":false});
            var Q8;
            Q8=makeQuery(id+"F10.boolean.opBoolean","COPY",EDGE,{"derivedFrom":makeQuery(id+"F10.opExtrude","CAP_EDGE",EDGE,{"disambiguationData":[OSD([sQuery(id+"F9.wireOp",EDGE,"E54.top")])],"isStart":false})});
            var Q9;
            Q9=makeQuery(id+"F10.boolean.opBoolean","COPY",EDGE,{"derivedFrom":makeQuery(id+"F10.opExtrude","CAP_EDGE",EDGE,{"disambiguationData":[OSD([sQuery(id+"F9.wireOp",EDGE,"E54.bottom")])],"isStart":false})});
            var Q10;
            Q10=makeQuery(id+"F10.boolean.opBoolean","COPY",EDGE,{"derivedFrom":makeQuery(id+"F10.opExtrude","CAP_EDGE",EDGE,{"disambiguationData":[OSD([sQuery(id+"F9.wireOp",EDGE,"E53.bottom")])],"isStart":false})});
            var Q11;
            Q11=makeQuery(id+"F10.boolean.opBoolean","COPY",EDGE,{"derivedFrom":makeQuery(id+"F10.opExtrude","CAP_EDGE",EDGE,{"disambiguationData":[OSD([sQuery(id+"F9.wireOp",EDGE,"E53.top")])],"isStart":false})});
            var Q12;
            Q12=makeQuery(id+"F4.opExtrude","CAP_EDGE",EDGE,{"disambiguationData":[OSD([sQuery(id+"F3.wireOp",EDGE,"E36.MirrorCS")])],"isStart":true});
            var Q13;
            Q13=makeQuery(id+"F4.opExtrude","CAP_EDGE",EDGE,{"disambiguationData":[OSD([sQuery(id+"F3.wireOp",EDGE,"E20")])],"isStart":true});
            var Q14;
            Q14=makeQuery(id+"F4.opExtrude","CAP_EDGE",EDGE,{"disambiguationData":[OSD([sQuery(id+"F3.wireOp",EDGE,"E19")])],"isStart":true});
            var Q15;
            Q15=makeQuery(id+"F4.opExtrude","CAP_EDGE",EDGE,{"disambiguationData":[OSD([sQuery(id+"F3.wireOp",EDGE,"E23.MirrorCS")])],"isStart":true});
            var Q16;
            Q16=makeQuery(id+"F4.opExtrude","CAP_EDGE",EDGE,{"disambiguationData":[OSD([sQuery(id+"F3.wireOp",EDGE,"E35.MirrorCS")])],"isStart":true});
            var Q17;
            Q17=makeQuery(id+"F4.opExtrude","CAP_EDGE",EDGE,{"disambiguationData":[OSD([sQuery(id+"F3.wireOp",EDGE,"E33.MirrorCS")])],"isStart":true});
            var Q18;
            Q18=makeQuery(id+"F4.opExtrude","CAP_EDGE",EDGE,{"disambiguationData":[OSD([sQuery(id+"F3.wireOp",EDGE,"E34.MirrorCS")])],"isStart":true});
            var Q19;
            Q19=makeQuery(id+"F4.opExtrude","CAP_EDGE",EDGE,{"disambiguationData":[OSD([sQuery(id+"F3.wireOp",EDGE,"E24.MirrorCS")])],"isStart":true});
            fillet(context, id + "F17", {"entities" : qUnion([Q0, Q1, Q2, Q3, Q4, Q5, Q6, Q7, Q8, Q9, Q10, Q11, Q12, Q13, Q14, Q15, Q16, Q17, Q18, Q19]), "radius" : 1 * mm, "tangentPropagation" : true, "allowEdgeOverflow" : false});
        }
        {
            var Q0;
            Q0=makeQuery(id+"F1.opExtrude","CAP_EDGE",EDGE,{"disambiguationData":[OSD([sQuery(id+"F0.wireOp",EDGE,"E0.bottom")])],"isStart":false});
            fillet(context, id + "F18", {"entities" : qUnion([Q0]), "radius" : 1 * mm, "tangentPropagation" : true, "allowEdgeOverflow" : false});
        }
        {
            var Q0;
            {var subQ0=sQuery(id+"F3.wireOp",EDGE,"E28.MirrorCS");var subQ1=sQuery(id+"F3.wireOp",EDGE,"E15");var subQ2=sQuery(id+"F0.wireOp",EDGE,"E0.right");var subQ4=sQuery(id+"F3.wireOp",EDGE,"E29.MirrorCS");var subQ5=sQuery(id+"F0.wireOp",EDGE,"E6");var subQ7=makeQuery(id+"F8.opShell","OFFSET_EDGE",EDGE,{"disambiguationData":[OSD([subQ2,subQ5,subQ1,subQ0,subQ4])]});Q0=makeQuery(id+"F12.boolean.opBoolean","MERGE",EDGE,{"derivedFrom":[makeQuery(id+"F10.boolean.opBoolean","SPLIT",EDGE,{"disambiguationData":[TD([makeQuery(id+"F10.opExtrude","SWEPT_FACE",FACE,{"disambiguationData":[OSD([sQuery(id+"F9.wireOp",EDGE,"E53.top")])]})])],"derivedFrom":subQ7}),makeQuery(id+"F10.boolean.opBoolean","SPLIT",EDGE,{"disambiguationData":[TD([makeQuery(id+"F10.opExtrude","SWEPT_FACE",FACE,{"disambiguationData":[OSD([sQuery(id+"F9.wireOp",EDGE,"E54.bottom")])]})])],"derivedFrom":subQ7}),makeQuery(id+"F10.boolean.opBoolean","SPLIT",EDGE,{"disambiguationData":[TD([makeQuery(id+"F10.opExtrude","SWEPT_FACE",FACE,{"disambiguationData":[OSD([sQuery(id+"F9.wireOp",EDGE,"E53.bottom")])]})])],"derivedFrom":subQ7}),makeQuery(id+"F12.opExtrude","SWEPT_EDGE",EDGE,{"disambiguationData":[OSD([sQuery(id+"F11.wireOp",EDGE,"E56.8"),sQuery(id+"F11.wireOp",EDGE,"E57")])]})]});}
            var Q1;
            {var subQ0=sQuery(id+"F3.wireOp",EDGE,"E39.MirrorCS");var subQ1=sQuery(id+"F3.wireOp",EDGE,"E25.MirrorCS");var subQ2=sQuery(id+"F0.wireOp",EDGE,"E0.bottom");var subQ4=sQuery(id+"F3.wireOp",EDGE,"E29.MirrorCS");var subQ5=sQuery(id+"F0.wireOp",EDGE,"E6");var subQ7=makeQuery(id+"F8.opShell","OFFSET_EDGE",EDGE,{"disambiguationData":[OSD([subQ2,subQ5,subQ1,subQ4,subQ0])]});Q1=makeQuery(id+"F12.boolean.opBoolean","MERGE",EDGE,{"derivedFrom":[makeQuery(id+"F10.boolean.opBoolean","SPLIT",EDGE,{"disambiguationData":[TD([makeQuery(id+"F10.opExtrude","SWEPT_FACE",FACE,{"disambiguationData":[OSD([sQuery(id+"F9.wireOp",EDGE,"E53.top")])]})])],"derivedFrom":subQ7}),makeQuery(id+"F10.boolean.opBoolean","SPLIT",EDGE,{"disambiguationData":[TD([makeQuery(id+"F10.opExtrude","SWEPT_FACE",FACE,{"disambiguationData":[OSD([sQuery(id+"F9.wireOp",EDGE,"E54.bottom")])]})])],"derivedFrom":subQ7}),makeQuery(id+"F10.boolean.opBoolean","SPLIT",EDGE,{"disambiguationData":[TD([makeQuery(id+"F10.opExtrude","SWEPT_FACE",FACE,{"disambiguationData":[OSD([sQuery(id+"F9.wireOp",EDGE,"E53.bottom")])]})])],"derivedFrom":subQ7}),makeQuery(id+"F12.opExtrude","SWEPT_EDGE",EDGE,{"disambiguationData":[OSD([sQuery(id+"F11.wireOp",EDGE,"E56.4"),sQuery(id+"F11.wireOp",EDGE,"E57")])]})]});}
            var Q2;
            {var subQ0=sQuery(id+"F3.wireOp",EDGE,"E28.MirrorCS");var subQ1=sQuery(id+"F3.wireOp",EDGE,"E15");var subQ2=sQuery(id+"F0.wireOp",EDGE,"E0.right");var subQ4=sQuery(id+"F3.wireOp",EDGE,"E11");var subQ5=sQuery(id+"F0.wireOp",EDGE,"E5");var subQ7=makeQuery(id+"F8.opShell","OFFSET_EDGE",EDGE,{"disambiguationData":[OSD([subQ2,subQ5,subQ4,subQ1,subQ0])]});Q2=makeQuery(id+"F12.boolean.opBoolean","MERGE",EDGE,{"derivedFrom":[makeQuery(id+"F10.boolean.opBoolean","SPLIT",EDGE,{"disambiguationData":[TD([makeQuery(id+"F10.opExtrude","SWEPT_FACE",FACE,{"disambiguationData":[OSD([sQuery(id+"F9.wireOp",EDGE,"E53.top")])]})])],"derivedFrom":subQ7}),makeQuery(id+"F10.boolean.opBoolean","SPLIT",EDGE,{"disambiguationData":[TD([makeQuery(id+"F10.opExtrude","SWEPT_FACE",FACE,{"disambiguationData":[OSD([sQuery(id+"F9.wireOp",EDGE,"E54.bottom")])]})])],"derivedFrom":subQ7}),makeQuery(id+"F10.boolean.opBoolean","SPLIT",EDGE,{"disambiguationData":[TD([makeQuery(id+"F10.opExtrude","SWEPT_FACE",FACE,{"disambiguationData":[OSD([sQuery(id+"F9.wireOp",EDGE,"E53.bottom")])]})])],"derivedFrom":subQ7}),makeQuery(id+"F12.opExtrude","SWEPT_EDGE",EDGE,{"disambiguationData":[OSD([sQuery(id+"F11.wireOp",EDGE,"E56.8"),sQuery(id+"F11.wireOp",EDGE,"E60")])]})]});}
            var Q3;
            {var subQ0=sQuery(id+"F3.wireOp",EDGE,"E37.MirrorCS");var subQ1=sQuery(id+"F3.wireOp",EDGE,"E16");var subQ2=sQuery(id+"F0.wireOp",EDGE,"E0.top");var subQ4=sQuery(id+"F3.wireOp",EDGE,"E11");var subQ5=sQuery(id+"F0.wireOp",EDGE,"E5");var subQ7=makeQuery(id+"F8.opShell","OFFSET_EDGE",EDGE,{"disambiguationData":[OSD([subQ2,subQ5,subQ4,subQ1,subQ0])]});Q3=makeQuery(id+"F12.boolean.opBoolean","MERGE",EDGE,{"derivedFrom":[makeQuery(id+"F10.boolean.opBoolean","SPLIT",EDGE,{"disambiguationData":[TD([makeQuery(id+"F10.opExtrude","SWEPT_FACE",FACE,{"disambiguationData":[OSD([sQuery(id+"F9.wireOp",EDGE,"E53.top")])]})])],"derivedFrom":subQ7}),makeQuery(id+"F10.boolean.opBoolean","SPLIT",EDGE,{"disambiguationData":[TD([makeQuery(id+"F10.opExtrude","SWEPT_FACE",FACE,{"disambiguationData":[OSD([sQuery(id+"F9.wireOp",EDGE,"E54.bottom")])]})])],"derivedFrom":subQ7}),makeQuery(id+"F10.boolean.opBoolean","SPLIT",EDGE,{"disambiguationData":[TD([makeQuery(id+"F10.opExtrude","SWEPT_FACE",FACE,{"disambiguationData":[OSD([sQuery(id+"F9.wireOp",EDGE,"E53.bottom")])]})])],"derivedFrom":subQ7}),makeQuery(id+"F12.opExtrude","SWEPT_EDGE",EDGE,{"disambiguationData":[OSD([sQuery(id+"F11.wireOp",EDGE,"E56.12"),sQuery(id+"F11.wireOp",EDGE,"E60")])]})]});}
            var Q4;
            {var subQ0=sQuery(id+"F3.wireOp",EDGE,"E37.MirrorCS");var subQ1=sQuery(id+"F3.wireOp",EDGE,"E16");var subQ2=sQuery(id+"F0.wireOp",EDGE,"E0.top");var subQ4=sQuery(id+"F3.wireOp",EDGE,"E49.MirrorCS");var subQ5=sQuery(id+"F0.wireOp",EDGE,"E4");var subQ7=makeQuery(id+"F8.opShell","OFFSET_EDGE",EDGE,{"disambiguationData":[OSD([subQ2,subQ5,subQ1,subQ0,subQ4])]});Q4=makeQuery(id+"F12.boolean.opBoolean","MERGE",EDGE,{"derivedFrom":[makeQuery(id+"F10.boolean.opBoolean","SPLIT",EDGE,{"disambiguationData":[TD([makeQuery(id+"F10.opExtrude","SWEPT_FACE",FACE,{"disambiguationData":[OSD([sQuery(id+"F9.wireOp",EDGE,"E53.top")])]})])],"derivedFrom":subQ7}),makeQuery(id+"F10.boolean.opBoolean","SPLIT",EDGE,{"disambiguationData":[TD([makeQuery(id+"F10.opExtrude","SWEPT_FACE",FACE,{"disambiguationData":[OSD([sQuery(id+"F9.wireOp",EDGE,"E54.bottom")])]})])],"derivedFrom":subQ7}),makeQuery(id+"F10.boolean.opBoolean","SPLIT",EDGE,{"disambiguationData":[TD([makeQuery(id+"F10.opExtrude","SWEPT_FACE",FACE,{"disambiguationData":[OSD([sQuery(id+"F9.wireOp",EDGE,"E53.bottom")])]})])],"derivedFrom":subQ7}),makeQuery(id+"F12.opExtrude","SWEPT_EDGE",EDGE,{"disambiguationData":[OSD([sQuery(id+"F11.wireOp",EDGE,"E56.12"),sQuery(id+"F11.wireOp",EDGE,"E59")])]})]});}
            var Q5;
            {var subQ0=sQuery(id+"F3.wireOp",EDGE,"E44.MirrorCS");var subQ1=sQuery(id+"F3.wireOp",EDGE,"E45.MirrorCS");var subQ2=sQuery(id+"F0.wireOp",EDGE,"E0.left");var subQ4=sQuery(id+"F3.wireOp",EDGE,"E49.MirrorCS");var subQ5=sQuery(id+"F0.wireOp",EDGE,"E4");var subQ7=makeQuery(id+"F8.opShell","OFFSET_EDGE",EDGE,{"disambiguationData":[OSD([subQ2,subQ5,subQ1,subQ0,subQ4])]});Q5=makeQuery(id+"F12.boolean.opBoolean","MERGE",EDGE,{"derivedFrom":[makeQuery(id+"F10.boolean.opBoolean","SPLIT",EDGE,{"disambiguationData":[TD([makeQuery(id+"F10.opExtrude","SWEPT_FACE",FACE,{"disambiguationData":[OSD([sQuery(id+"F9.wireOp",EDGE,"E53.top")])]})])],"derivedFrom":subQ7}),makeQuery(id+"F10.boolean.opBoolean","SPLIT",EDGE,{"disambiguationData":[TD([makeQuery(id+"F10.opExtrude","SWEPT_FACE",FACE,{"disambiguationData":[OSD([sQuery(id+"F9.wireOp",EDGE,"E54.bottom")])]})])],"derivedFrom":subQ7}),makeQuery(id+"F10.boolean.opBoolean","SPLIT",EDGE,{"disambiguationData":[TD([makeQuery(id+"F10.opExtrude","SWEPT_FACE",FACE,{"disambiguationData":[OSD([sQuery(id+"F9.wireOp",EDGE,"E53.bottom")])]})])],"derivedFrom":subQ7}),makeQuery(id+"F12.opExtrude","SWEPT_EDGE",EDGE,{"disambiguationData":[OSD([sQuery(id+"F11.wireOp",EDGE,"E56.2"),sQuery(id+"F11.wireOp",EDGE,"E59")])]})]});}
            var Q6;
            {var subQ0=sQuery(id+"F3.wireOp",EDGE,"E44.MirrorCS");var subQ1=sQuery(id+"F3.wireOp",EDGE,"E45.MirrorCS");var subQ2=sQuery(id+"F0.wireOp",EDGE,"E0.left");var subQ4=sQuery(id+"F3.wireOp",EDGE,"E42.MirrorCS");var subQ5=sQuery(id+"F0.wireOp",EDGE,"E3");var subQ7=makeQuery(id+"F8.opShell","OFFSET_EDGE",EDGE,{"disambiguationData":[OSD([subQ2,subQ5,subQ1,subQ0,subQ4])]});Q6=makeQuery(id+"F12.boolean.opBoolean","MERGE",EDGE,{"derivedFrom":[makeQuery(id+"F10.boolean.opBoolean","SPLIT",EDGE,{"disambiguationData":[TD([makeQuery(id+"F10.opExtrude","SWEPT_FACE",FACE,{"disambiguationData":[OSD([sQuery(id+"F9.wireOp",EDGE,"E53.top")])]})])],"derivedFrom":subQ7}),makeQuery(id+"F10.boolean.opBoolean","SPLIT",EDGE,{"disambiguationData":[TD([makeQuery(id+"F10.opExtrude","SWEPT_FACE",FACE,{"disambiguationData":[OSD([sQuery(id+"F9.wireOp",EDGE,"E54.bottom")])]})])],"derivedFrom":subQ7}),makeQuery(id+"F10.boolean.opBoolean","SPLIT",EDGE,{"disambiguationData":[TD([makeQuery(id+"F10.opExtrude","SWEPT_FACE",FACE,{"disambiguationData":[OSD([sQuery(id+"F9.wireOp",EDGE,"E53.bottom")])]})])],"derivedFrom":subQ7}),makeQuery(id+"F12.opExtrude","SWEPT_EDGE",EDGE,{"disambiguationData":[OSD([sQuery(id+"F11.wireOp",EDGE,"E56.2"),sQuery(id+"F11.wireOp",EDGE,"E58")])]})]});}
            var Q7;
            {var subQ0=sQuery(id+"F3.wireOp",EDGE,"E39.MirrorCS");var subQ1=sQuery(id+"F3.wireOp",EDGE,"E25.MirrorCS");var subQ2=sQuery(id+"F0.wireOp",EDGE,"E0.bottom");var subQ4=sQuery(id+"F3.wireOp",EDGE,"E42.MirrorCS");var subQ5=sQuery(id+"F0.wireOp",EDGE,"E3");var subQ7=makeQuery(id+"F8.opShell","OFFSET_EDGE",EDGE,{"disambiguationData":[OSD([subQ2,subQ5,subQ1,subQ0,subQ4])]});Q7=makeQuery(id+"F12.boolean.opBoolean","MERGE",EDGE,{"derivedFrom":[makeQuery(id+"F10.boolean.opBoolean","SPLIT",EDGE,{"disambiguationData":[TD([makeQuery(id+"F10.opExtrude","SWEPT_FACE",FACE,{"disambiguationData":[OSD([sQuery(id+"F9.wireOp",EDGE,"E53.top")])]})])],"derivedFrom":subQ7}),makeQuery(id+"F10.boolean.opBoolean","SPLIT",EDGE,{"disambiguationData":[TD([makeQuery(id+"F10.opExtrude","SWEPT_FACE",FACE,{"disambiguationData":[OSD([sQuery(id+"F9.wireOp",EDGE,"E54.bottom")])]})])],"derivedFrom":subQ7}),makeQuery(id+"F10.boolean.opBoolean","SPLIT",EDGE,{"disambiguationData":[TD([makeQuery(id+"F10.opExtrude","SWEPT_FACE",FACE,{"disambiguationData":[OSD([sQuery(id+"F9.wireOp",EDGE,"E53.bottom")])]})])],"derivedFrom":subQ7}),makeQuery(id+"F12.opExtrude","SWEPT_EDGE",EDGE,{"disambiguationData":[OSD([sQuery(id+"F11.wireOp",EDGE,"E56.4"),sQuery(id+"F11.wireOp",EDGE,"E58")])]})]});}
            fillet(context, id + "F19", {"entities" : qUnion([Q0, Q1, Q2, Q3, Q4, Q5, Q6, Q7]), "radius" : 1 * mm, "tangentPropagation" : true, "allowEdgeOverflow" : false});
        }
    });
